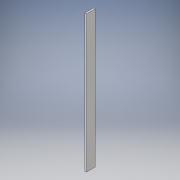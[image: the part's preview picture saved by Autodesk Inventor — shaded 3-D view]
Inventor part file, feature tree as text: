
AUTODESK INVENTOR PART (.ipt)
format: ipt  version: 2017 (Build 210142000, 142)  size: 92,160 bytes
history: native  units: in
note: dims shown in document units (in); Inventor stores cm internally (conversion verified against a paired STEP export)
features: extrude x1, sketch x1
ambient origin geometry x8: Origin, YZ Plane, XZ Plane, XY Plane, X Axis, Y Axis, Z Axis, Center Point
bodies: Solid1 (feature_tree)
feature tree (2):
  extrude  "Extrusion1"  Depth=78.8675in
  sketch  "Sketch1"  dims[d0=1.0in d1=78.8675in d2=5.0in d3=0.0in]
